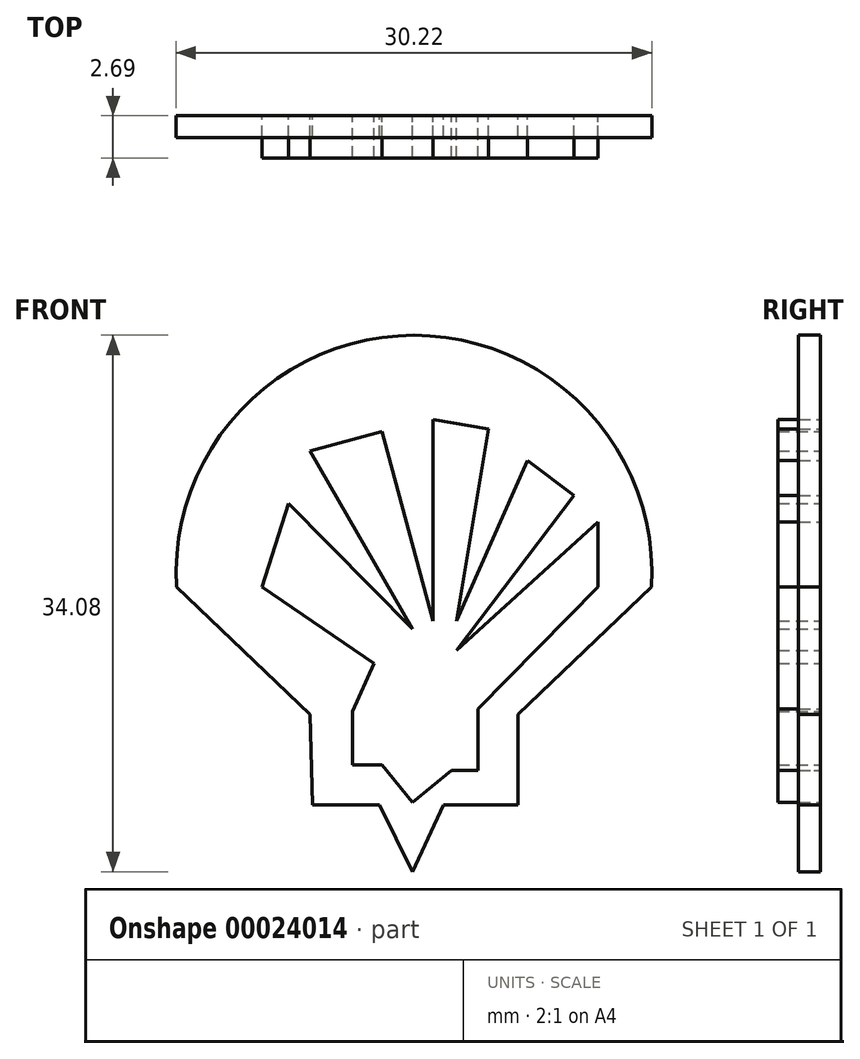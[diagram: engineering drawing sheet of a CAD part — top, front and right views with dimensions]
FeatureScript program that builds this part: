
annotation { "Feature Type Name" : "Feature", "Feature Type Description" : "" }
export const myFeature = defineFeature(function(context is Context, id is Id, definition is map)
    precondition{}
    {
        {
            var Q0;
            Q0=qCreatedBy(makeId("Front.planeOp"),FACE);
            var sketch = newSketch(context, id + "F0", { "sketchPlane" : qUnion([Q0])});
            skArc(sketch, "E0", {"start": v(15.16, 0) * mm, "mid": v(0.08, 15.99) * mm, "end": v(-15, 0) * mm});
            skLineSegment(sketch, "E1", {"start": v(-15, 0) * mm, "end": v(-6.53, -8.1) * mm});
            skLineSegment(sketch, "E2", {"start": v(15.16, 0) * mm, "end": v(6.7, -8.1) * mm});
            skLineSegment(sketch, "E3", {"start": v(6.7, -8.1) * mm, "end": v(6.7, -13.85) * mm});
            skLineSegment(sketch, "E4", {"start": v(6.7, -13.85) * mm, "end": v(1.95, -13.85) * mm});
            skLineSegment(sketch, "E5", {"start": v(1.95, -13.85) * mm, "end": v(0, -18.09) * mm});
            skLineSegment(sketch, "E6", {"start": v(0, -18.09) * mm, "end": v(-2.12, -13.85) * mm});
            skLineSegment(sketch, "E7", {"start": v(-2.12, -13.85) * mm, "end": v(-6.36, -13.85) * mm});
            skLineSegment(sketch, "E8", {"start": v(-6.36, -13.85) * mm, "end": v(-6.53, -8.1) * mm});
            skSolve(sketch);
        }
        {
            var Q0;
            Q0=qCreatedBy(makeId("Front.planeOp"),FACE);
            var sketch = newSketch(context, id + "F1", { "sketchPlane" : qUnion([Q0])});
            skLineSegment(sketch, "E9", {"start": v(-3.82, -7.92) * mm, "end": v(-3.82, -11.31) * mm});
            skLineSegment(sketch, "E10", {"start": v(-3.82, -11.31) * mm, "end": v(-1.95, -11.31) * mm});
            skLineSegment(sketch, "E11", {"start": v(-1.95, -11.31) * mm, "end": v(0, -13.68) * mm});
            skLineSegment(sketch, "E12", {"start": v(0, -13.68) * mm, "end": v(2.47, -11.65) * mm});
            skLineSegment(sketch, "E13", {"start": v(2.47, -11.65) * mm, "end": v(4.15, -11.65) * mm});
            skLineSegment(sketch, "E14", {"start": v(4.15, -11.65) * mm, "end": v(4.15, -7.75) * mm});
            skLineSegment(sketch, "E15", {"start": v(4.15, -7.75) * mm, "end": v(11.78, 0) * mm});
            skLineSegment(sketch, "E16", {"start": v(11.78, 0) * mm, "end": v(11.78, 4.11) * mm});
            skLineSegment(sketch, "E17", {"start": v(11.78, 4.11) * mm, "end": v(2.8, -4.02) * mm});
            skLineSegment(sketch, "E18", {"start": v(2.8, -4.02) * mm, "end": v(10.25, 5.8) * mm});
            skLineSegment(sketch, "E19", {"start": v(10.25, 5.8) * mm, "end": v(7.3, 8.04) * mm});
            skLineSegment(sketch, "E20", {"start": v(7.3, 8.04) * mm, "end": v(2.8, -2.16) * mm});
            skLineSegment(sketch, "E21", {"start": v(2.8, -2.16) * mm, "end": v(4.83, 10.04) * mm});
            skLineSegment(sketch, "E22", {"start": v(4.83, 10.04) * mm, "end": v(1.28, 10.63) * mm});
            skLineSegment(sketch, "E23", {"start": v(1.28, 10.63) * mm, "end": v(1.28, -2.16) * mm});
            skLineSegment(sketch, "E24", {"start": v(1.28, -2.16) * mm, "end": v(-1.95, 9.87) * mm});
            skLineSegment(sketch, "E25", {"start": v(-1.95, 9.87) * mm, "end": v(-6.53, 8.64) * mm});
            skLineSegment(sketch, "E26", {"start": v(-6.53, 8.64) * mm, "end": v(0, -2.67) * mm});
            skLineSegment(sketch, "E27", {"start": v(0, -2.67) * mm, "end": v(-7.88, 5.3) * mm});
            skLineSegment(sketch, "E28", {"start": v(-7.88, 5.3) * mm, "end": v(-9.58, 0) * mm});
            skLineSegment(sketch, "E29", {"start": v(-9.58, 0) * mm, "end": v(-2.46, -4.87) * mm});
            skLineSegment(sketch, "E30", {"start": v(-2.46, -4.87) * mm, "end": v(-3.82, -7.92) * mm});
            skSolve(sketch);
        }
        {
            var Q0;
            Q0=makeQuery(id+"F0.imprint","IMPRINT",FACE,{"disambiguationData":[TD([[makeQuery(id+"F0.imprint","IMPRINT",EDGE,{"derivedFrom":sQuery(id+"F0.wireOp",EDGE,"E0")}),1.0]])]});
            extrude(context, id + "F2", {"entities" : qUnion([Q0]), "depth" : 1.38 * mm});
        }
        {
            var Q0;
            Q0 = qSketchRegion(id + "F1", true);
            extrude(context, id + "F3", {"entities" : qUnion([Q0]), "depth" : 2.69 * mm});
        }
    });
